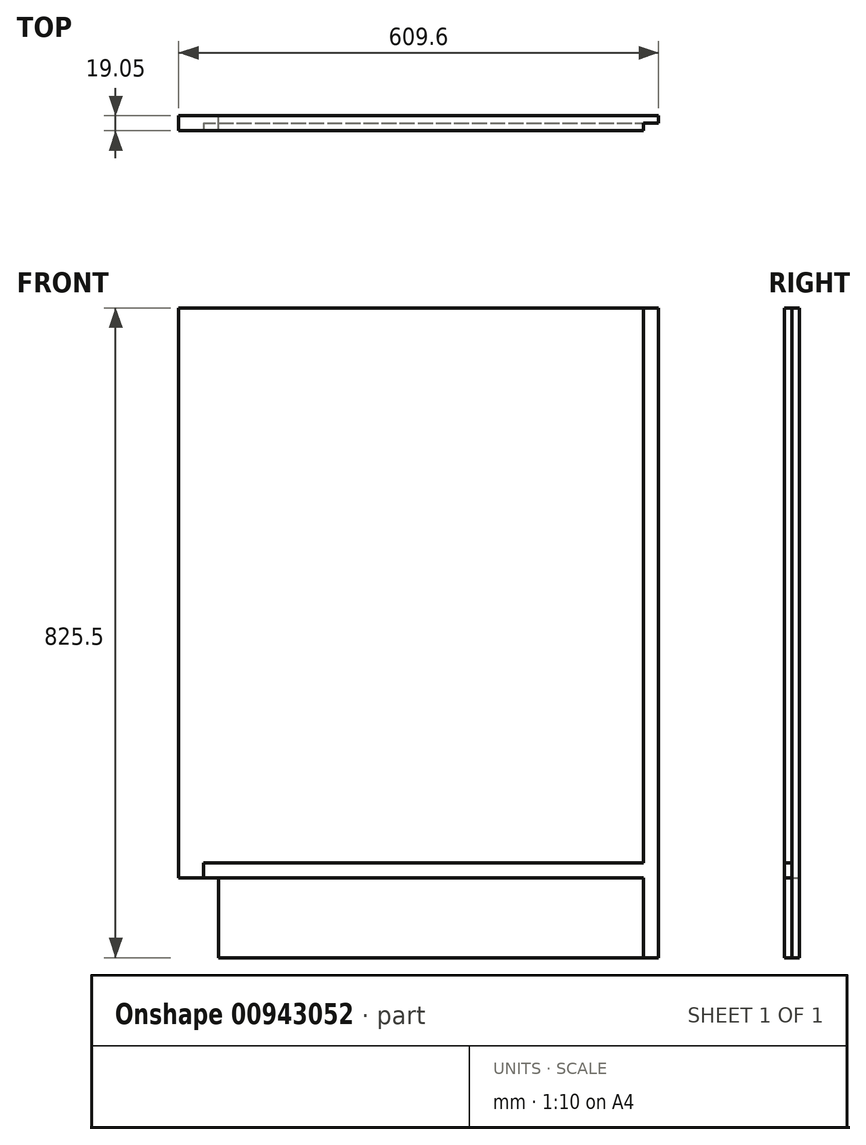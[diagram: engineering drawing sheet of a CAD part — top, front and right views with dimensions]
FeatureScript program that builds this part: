
annotation { "Feature Type Name" : "Feature", "Feature Type Description" : "" }
export const myFeature = defineFeature(function(context is Context, id is Id, definition is map)
    precondition{}
    {
        {
            var Q0;
            Q0=qCreatedBy(makeId("Front.planeOp"),FACE);
            var sketch = newSketch(context, id + "F0", { "sketchPlane" : qUnion([Q0])});
            skLineSegment(sketch, "E0.bottom", {"start": v(0, 0) * mm, "end": v(-558.8, 0) * mm});
            skLineSegment(sketch, "E0.top", {"start": v(0, 825.5) * mm, "end": v(-609.6, 825.5) * mm});
            skLineSegment(sketch, "E0.left", {"start": v(0, 0) * mm, "end": v(0, 825.5) * mm});
            skLineSegment(sketch, "E0.right", {"start": v(-609.6, 101.6) * mm, "end": v(-609.6, 825.5) * mm});
            skLineSegment(sketch, "E1", {"start": v(-609.6, 101.6) * mm, "end": v(-558.8, 101.6) * mm});
            skLineSegment(sketch, "E2", {"start": v(-558.8, 101.6) * mm, "end": v(-558.8, 0) * mm});
            skSolve(sketch);
        }
        {
            var Q0;
            Q0=makeQuery(id+"F0.imprint","IMPRINT",FACE,{"disambiguationData":[TD([[makeQuery(id+"F0.imprint","IMPRINT",EDGE,{"derivedFrom":sQuery(id+"F0.wireOp",EDGE,"E0.bottom")}),-1.0]])]});
            extrude(context, id + "F1", {"entities" : qUnion([Q0]), "depth" : 19.05 * mm, "offsetDistance" : 25.4 * mm});
        }
        {
            var Q0;
            Q0=makeQuery(id+"F1.opExtrude","CAP_FACE",FACE,{"disambiguationData":[OSD([sQuery(id+"F0.wireOp",EDGE,"E0.bottom"),sQuery(id+"F0.wireOp",EDGE,"E0.top"),sQuery(id+"F0.wireOp",EDGE,"E0.left"),sQuery(id+"F0.wireOp",EDGE,"E0.right"),sQuery(id+"F0.wireOp",EDGE,"E1"),sQuery(id+"F0.wireOp",EDGE,"E2")])],"isStart":false});
            var sketch = newSketch(context, id + "F2", { "sketchPlane" : qUnion([Q0])});
            skLineSegment(sketch, "E3", {"start": v(-19.05, 825.5) * mm, "end": v(0, 825.5) * mm});
            skLineSegment(sketch, "E4", {"start": v(0, 0) * mm, "end": v(-19.05, 0) * mm});
            skLineSegment(sketch, "E5", {"start": v(-19.05, 0) * mm, "end": v(-19.05, 101.6) * mm});
            skLineSegment(sketch, "E6", {"start": v(-19.05, 101.6) * mm, "end": v(-577.85, 101.6) * mm});
            skLineSegment(sketch, "E7", {"start": v(-577.85, 101.6) * mm, "end": v(-577.85, 120.65) * mm});
            skLineSegment(sketch, "E8", {"start": v(-577.85, 120.65) * mm, "end": v(-19.05, 120.65) * mm});
            skLineSegment(sketch, "E9", {"start": v(-19.05, 120.65) * mm, "end": v(-19.05, 825.5) * mm});
            skSolve(sketch);
        }
        {
            var Q0;
            Q0 = qSketchRegion(id + "F2", true);
            var Q1;
            Q1=makeQuery(id+"F2.imprint","IMPRINT",FACE,{"disambiguationData":[TD([[makeQuery(id+"F2.imprint","IMPRINT",EDGE,{"derivedFrom":sQuery(id+"F2.wireOp",EDGE,"E3")}),1.0]])]});
            extrude(context, id + "F3", {"entities" : qUnion([Q0, Q1]), "operationType" : NewBodyOperationType.REMOVE, "oppositeDirection" : true, "depth" : 9.52 * mm, "offsetDistance" : 25.4 * mm});
        }
    });
